# Revit family: PRE050032-FR
name_source: partatom
category: Accessoire de canalisation
revit_build: Autodesk Revit 2017 (Build: 20160225_1515(x64)
units: mm (PartAtom-declared; Revit-internal decimal feet)

## family parameters
Basée sur le plan de construction = Non
Cote de connecteur circulaire = Utiliser le diamètre
Couper avec des vides une fois chargée = Non
Partagée = Non
Toujours verticalement = Oui
Type d'élément = Normal

## types (1)
- 75110 Presto Sanifirst Mitigeur thermostatique de bain douche hospitalier choc thermique
    Adresse = 7, RUE RACINE - 92542 MONTROUGE CEDEX FRANCE
    Description = Mitigeur thermostatique de bain-douche entraxe 150mm mural. Un volant double débit et un volant spécial choc thermique bloqué à 38°C/41°C (deux butées) avec système de déverrouillage sécurisé sans changer de volant et accessible uniquement par les personnes des services techniques. Raccords excentrés M1/2 avec rosaces chromées et joints filtres. Arrivée EF/ECS équipée de clapet anti-retour, sortie de douche M’1/2. Tête céramique ½ tour pour le réglage du débit et cartouche thermostatique NF pour le réglage de la température. Robinetterie équipée d’origine avec un brise-jet étoile M28X1. Corps et volants en laiton poli chromé. Garantie 3 ans pour la cartouche thermostatique et 10 ans pour le reste de la robinetterie. Marque Sanifirst type mitigeur thermostatique de bain-douche entraxe 150mm REF : 75110 ou équivalent approuvé.
    Diamètre Nominal = 15 mm  [stored 0.0492126 ft]
    Fabricant = LES ROBINETS PRESTO S.A.
    Finition = Corps et volants en laiton poli chromé
    Flux = 0.1 L/s
    Fonction = Mitigeur thermostatique de bain-douche entraxe 150mm mural, choc thermique.

Organe de manœuvre : Volants laiton

Référence : 75110
    Garantie = 10 ans contre tout vice de fabrication / 3 ans pour la cartouche thermostatique
    HC = 30 mm  [stored 0.0984252 ft]
    Hauteur = 60 mm  [stored 0.19685 ft]
    LC = 30 mm  [stored 0.0984252 ft]
    Largeur = 259 mm
    Lien CCTP = http://www.prestodatashare.com
    Lien fiche produit = http://www.prestodatashare.com
    Lien notice d'utilisation = http://www.prestodatashare.com
    Matériau = Laiton poli chromé
    Modèle = 75110 Presto Sanifirst Mitigeur thermostatique de bain douche hospitalier choc thermique
    Perte de charge = 0.0 Pa
    Polantis code = PRE050032-FR
    Pression = 3 bars - Eviter les écarts de pressions supérieurs à 1 bar entre l'eau chaude et l'eau froide
    Profondeur = 156 mm  [stored 0.511811 ft]
    Raccordement = EP G'3/4 livré avec rosaces et raccords excentrés M G'1/2 M G'3/4
    Reference = 75110
    URL = http://www.prestodatashare.com
    URL Fabricant = http://www.prestodatashare.com
    Variantes = 75110

note: [stored X ft] marks values corroborated as IEEE doubles in the binary element streams (Revit-internal decimal feet)
